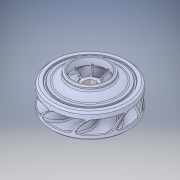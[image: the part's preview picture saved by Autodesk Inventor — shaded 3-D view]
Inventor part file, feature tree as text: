
AUTODESK INVENTOR PART (.ipt)
format: ipt  version: 2019 (Build 230136000, 136)  size: 6,988,800 bytes
history: native  units: mm
features: extrude x4, sketch x4, other x3
ambient origin geometry x8: Origin, YZ Plane, XZ Plane, XY Plane, X Axis, Y Axis, Z Axis, Center Point
bodies: Solid1 (feature_tree)
feature tree (11):
  other  "impeller modified.ipt"
  extrude  "Extrusion1"  Depth=10.0mm TaperAngle=0.0deg
  extrude  "Extrusion3"  Depth=12.5mm TaperAngle=0.0deg
  extrude  "Extrusion4"  Depth=10.0mm
  extrude  "Extrusion5"  [1 undecoded]
  other  "Solid1::impeller modified.ipt"
  other  "TaggingFeature1"
  sketch  "Sketch1"  dims[d0=7.5mm d1=10.0mm d2=0.0mm]
  sketch  "Sketch3"  dims[d6=10.15mm d7=12.5mm d8=0.0mm]
  sketch  "Sketch4"  dims[d9=10.0mm d10=0.0mm d11=6.1mm]
  sketch  "Sketch5"  dims[d12=10.0mm d13=0.0mm]
note: 1 required parameter value undecoded (feature->parameter linkage not recoverable at this tier; creation-order binding heuristic only, values carry confidence <= 0.55)
